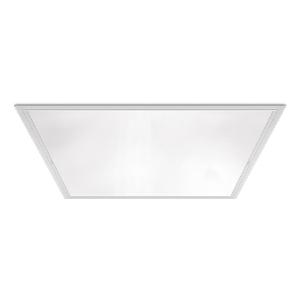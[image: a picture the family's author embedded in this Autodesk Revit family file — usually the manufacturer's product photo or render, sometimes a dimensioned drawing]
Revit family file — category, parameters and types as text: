
# Revit family: 3f_filippi_-_l_340_luce_diffusa_lgs_3f_filippi_-_23863_-_l_340_25w-840_dali_lgs_596x596
name_source: partatom
category: Lighting Fixtures
units: mm (PartAtom-declared; Revit-internal decimal feet)

## family parameters
Cut with Voids When Loaded = No
Host = Face
Light Source = No
Part Type = Normal
Room Calculation Point = No
Round Connector Dimension = Use Diameter
Shared = No

## types (1)
- 3F Filippi - L 340 Luce Diffusa LGS (1 x LED, 3785 lm, 29 W, 4000 K)
    Apparent Load = 29 VA
    Approval mark = ENEC
    CIE Flux Codes = 67 92 98 100 100
    Color Rendering = 80
    Color Temperature = 4000 K
    Control Gear = Electronic transformer
    Default Elevation = 1800 mm
    Description = ILLUMINOTECHNICAL
Luminous efficiency 100% (DLOR 100%, ULOR 0%).
Initial luminous flux of the luminaire 3785 lm.
Direct symmetric distribution.
Installation Interdistance Transv.D = 1.19 x hu - Long.D = 1.17 x hu.
Average luminance <1500 cd/m² for radial angles >65°.
Tabular UGR (CIE 117 - 4H-8H; S=0.25H; 70/50/20): RUG 16.4 - 16.4.
Beam angle: 87° - 86°.
Luminous efficacy 131 lm/W.
Lifetime (L93/B10): 30000 h. (tq+25°C)
Lifetime (L90/B10): 50000 h. (tq+25°C)
Lifetime (L85/B10): 80000 h. (tq+25°C)
Lifetime (L80/B10): 100000 h. (tq+25°C)
Sudden decreased luminous flux after 50000 hours: 0% (C0).
Photobiological safety in compliance with IEC/TR 62778: RG0 risk exempt, (IEC 62471).
In compliance with IEC/EN 62722-2-1 - IEC/EN 62717 standards.

SOURCE
Squared LED module 25W/840.
Energy efficiency class (UE 2019/2020 - UE 2019/2015): C.
CIE 13.3 Colour rendering index: CRI >80 (R9 <50%).
IES TM-30 Fidelity Index: Rf = 84 Rg = 95.
CCT nominal colour temperature 4000 K.
Colour initial tolerance (MacAdam): SDCM 3.

MECHANICAL
Housing in hot-galvanised steel, painted in white polyester.
Perimetral frame in white polycarbonate.
LGS micro-prismatic flat diffuser in transparent methacrylate (PMMA), multi-lenticular exterior, anti-glare.
Anti-glare opal polycarbonate filter for brightness uniformity.
Luminaire with limited surface temperature. - D - (EN 60598-2-24)
Dimensions: 596x596 mm, height 80 mm. Weight 4.4 kg.
IP40 protection degree.
Mechanical strength to impacts IK06 (1 joule).
Glow-wire test resistance 650°C.

ELECTRICAL
Wiring on a separate unit.
Halogen Free DALI-2 DATI (Parts 251, 252, 253), PUSH-DIM, electronic wiring 230V-50/60Hz, power factor 0.95 at full load, THD <25%, constant output current, SELV, class II, 1 driver, 1 DALI addresse.
Power of the luminaire 29 W.
CE - IEC 60598-1 - EN 60598-1.
SAFE FLICKER: PstLM=<1 and SVM=<0.4 (IEC TR 61547-1 and IEC TR 63158), to ensure a more comfortable and safe light.
Luminaire compliant with EN 60598-2-22 for power supply from a centralised emergency system CPSS (Central Power Supply System), not incorporated in the luminaire - high risk areas excluded. The default power and flux are 100% in AC and 100% in DC.
Ambient temperature from 0°C to +40°C.
Temperature class T6 max 85°C.
Relative humidity UR: <85%.

INSTALLATION
Lay-on or pull-up recessed fitting using frame accessory.
All accessories dedicated to this product are available on the Catalog and on our website www.3F-Filippi.com.

APPLICATIONS
Suitable product for food production plants (HACCP), IFS (Food Version 6), BRC (GSFS Food Version 7).
Environments: with VDTs, meeting rooms, offices.
Environments: architectural, commercial, staterooms, banks.
Environments where demanding visual tasks are performed and soft diffuse light is required for optimal visual comfort and total shielding of the light source.

LIGHT MANAGEMENT
Recommended minimum setting: 10%.
The luminaire, equipped with (DALI-2 DATI) driver, can be controlled manually with 3F Easy Dim technology or automatically/manually with wired or wireless DALI/D2D control systems.
The D2D driver guarantees interoperability with other devices with the same certification by making the following information available:
Device Data (Part 251), Energy Report (Part 252), Diagnosis & Maintenance (Part 253).
In electrical systems without a regulation system (manual or automatic) and DALI bus, a suitable jumper must be made on the DA-DA terminals of the appliance.

WARNING
Luminaire designed for disposal/recycling at end-of-life.
Replaceable (LED only) light source by a professional. Replaceable control gear by a professional.
    Height = 0 mm  [stored 0 ft]
    Lamp = 1 x LED
    Lamp Light Flux = 3785 lm
    Lamp Power = 29 W
    Lamp count = 1
    Length = 596 mm
    Lifetime = 50000 h
    Luminous efficacy = 131 lm/W
    Manufacturer = 3F Filippi
    ModVariant = No
    Model = 3F Filippi - 23863 - L 340 25W-840 DALI LGS 596x596
    Mounting Place = Ceiling
    Mounting Type = Recessed
    Number of Poles = 1
    OnlyDefault = Yes
    Power Factor = 1
    Product Name = 3F Filippi - L 340 Luce Diffusa LGS
    Product group = recessed luminaire
    ProductGroupID = 4
    Protection Class = Protection class II
    Protection Degree = IP 40
    RLX_Detail_Level = 1
    RLX_Emergency_Light_Flux = 0 lm
    RLX_Emergency_Type = 0
    RLX_Emergency_Type_DB = No
    RlxData = <blob elided: 156141 chars, md5=05eb8a6c>
    Socket = socket
    Standby Power = 0 W
    System Light Flux = 3785 lm
    System Power = 29 W
    Type Comments = Product without accessories
    Type Image = 3ffilippi_l_340_luce_diffusa_lgs.jpg
    URL = http://relux.com
    VarID = ---
    Voltage = 0 V
    Weight = 0.00 kg
    Width = 596 mm

note: [stored X ft] marks values corroborated as IEEE doubles in the binary element streams (Revit-internal decimal feet)

## geometry (parser evidence)
native form markers: Blend x4, Sweep x10
no freeform markers — native parametric forms only
